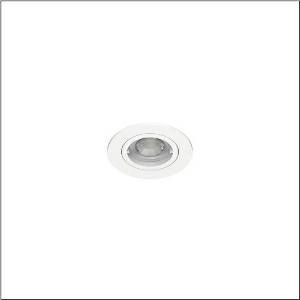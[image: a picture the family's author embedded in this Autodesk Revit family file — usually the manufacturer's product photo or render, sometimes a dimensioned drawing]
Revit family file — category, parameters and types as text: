
# Revit family: lunis_41_spot_51dt13ma42b
name_source: partatom
category: Lighting Fixtures
units: mm (PartAtom-declared; Revit-internal decimal feet)

## family parameters
Cut with Voids When Loaded = No
Host = Face
Light Source = No
Part Type = Normal
Room Calculation Point = No
Round Connector Dimension = Use Diameter
Shared = No

## types (1)
- Lunis 41 Spot (1 x LED, 600 lm, 4.6 W, 4000K)
    Apparent Load = 5 VA
    CIE Flux Codes = 87 97 99 100 100
    Color Rendering = 80
    Color Temperature = 4000K
    Default Elevation = 1800 mm
    Description = Lunis 41,  Spot, downlight, light emission: direct distribution, LED rated luminous flux: 600lm, light colour: 840, mains connection: 230V, AC, 50/60Hz, housing, round, of aluminium, coated, traffic white (RAL 9016), diameter: 88mm, recess depth: 54mm, protection rating (complete): IP20, protection rating (on room side): IP20, insulation class (complete): insulation class II (safety insulation), certification: CE, permissible ambient temperature for indoor applications: -20..+40°C, packaging unit: 1 piece
    Height = 0 mm  [stored 0 ft]
    Lamp = 1 x LED
    Lamp Light Flux = 600 lm
    Lamp Power = 4.6 W
    Lamp count = 1
    Length = 88 mm
    Luminous efficacy = 130 lm/W
    Manufacturer = Siteco
    ModVariant = No
    Model = 51DT13MA42B
    Mounting Place = Ceiling
    Mounting Type = Recessed
    Number of Poles = 1
    OnlyDefault = Yes
    Power Factor = 1
    Product Name = Lunis 41 Spot
    Product group = downlight
    ProductGroupID = 400
    Protection Class = Protection class II
    Protection Degree = IP 20
    RLX_Detail_Level = 1
    RLX_Emergency_Light_Flux = 0 lm
    RLX_Emergency_Type = 0
    RLX_Emergency_Type_DB = No
    RlxData = <blob elided: 9917 chars, md5=ec26f74a>
    Socket = socket
    Standby Power = 0 W
    System Light Flux = 600 lm
    System Power = 5 W
    Type Comments = Product without accessories
    Type Image = l_1345917.jpg
    URL = http://relux.com
    VarID = ---
    Voltage = 0 V
    Weight = 0.00 kg
    Width = 0 mm  [stored 0 ft]

note: [stored X ft] marks values corroborated as IEEE doubles in the binary element streams (Revit-internal decimal feet)

## geometry (parser evidence)
native form markers: Sweep x9
no freeform markers — native parametric forms only
